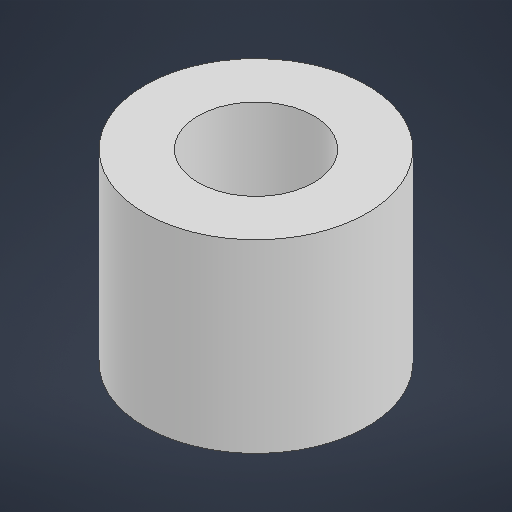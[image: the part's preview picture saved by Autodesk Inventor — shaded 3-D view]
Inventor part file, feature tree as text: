
AUTODESK INVENTOR PART (.ipt)
format: ipt  version: 2025.1 (Build 291241000, 241)  size: 390,656 bytes
history: native  units: mm
features: extrude x1, sketch x1
ambient origin geometry x8: Origin, YZ Plane, XZ Plane, XY Plane, X Axis, Y Axis, Z Axis, Center Point
bodies: Solid1 (feature_tree)
feature tree (2):
  extrude  "Extrusion1"  Depth=4.0mm
  sketch  "Sketch1"  dims[d0=4.8mm d1=2.5mm d2=4.0mm d3=0.0mm]
